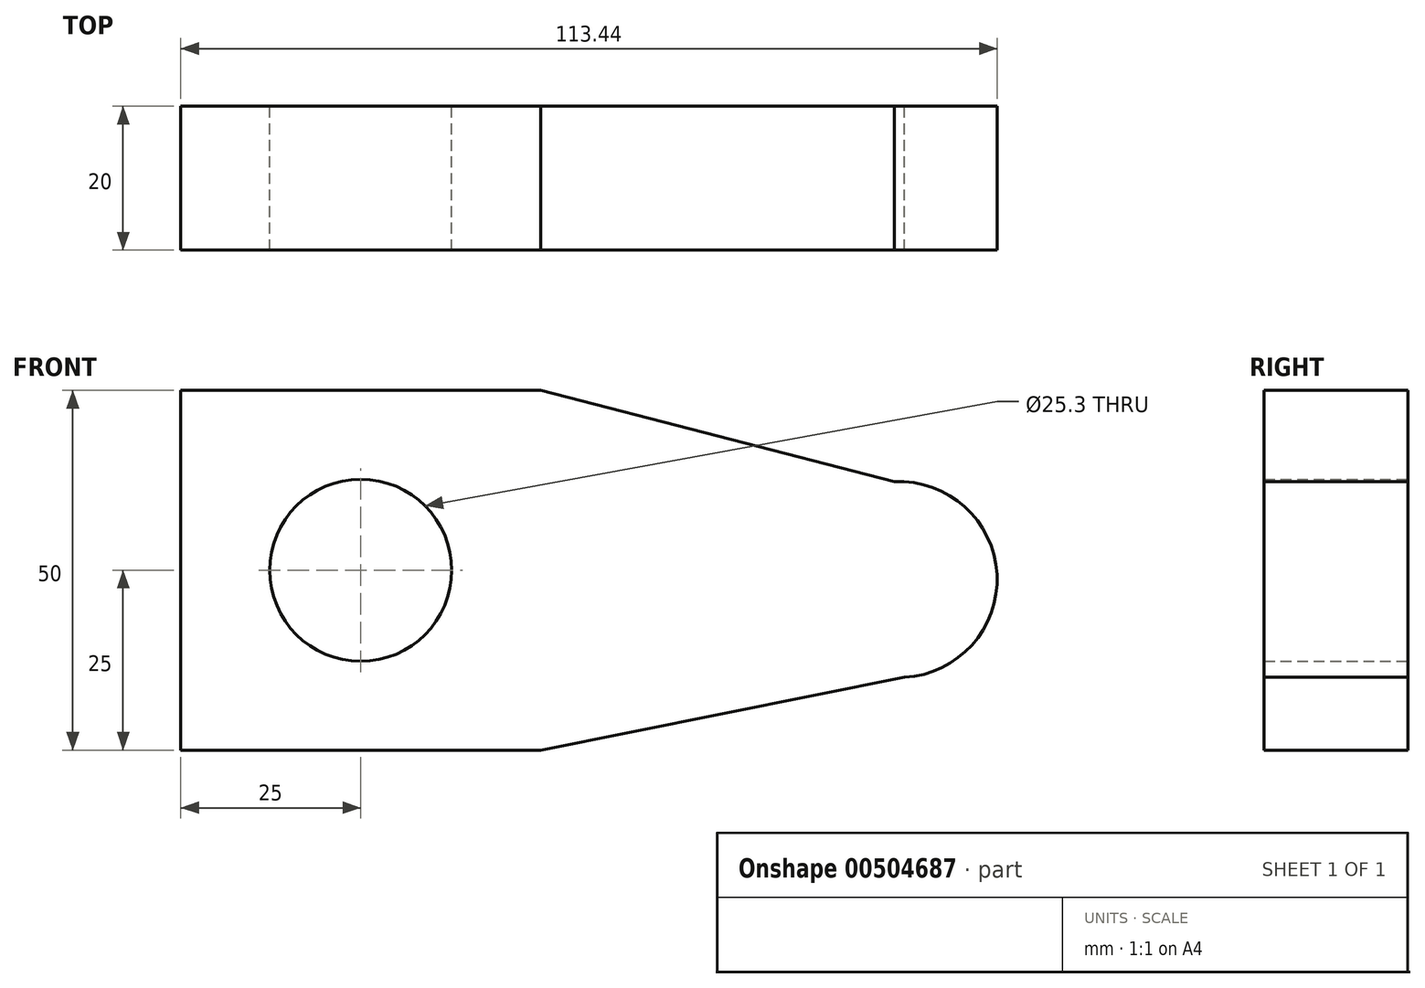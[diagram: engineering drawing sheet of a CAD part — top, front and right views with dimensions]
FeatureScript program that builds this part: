
annotation { "Feature Type Name" : "Feature", "Feature Type Description" : "" }
export const myFeature = defineFeature(function(context is Context, id is Id, definition is map)
    precondition{}
    {
        {
            var Q0;
            Q0=qCreatedBy(makeId("Front.planeOp"),FACE);
            var sketch = newSketch(context, id + "F0", { "sketchPlane" : qUnion([Q0])});
            skLineSegment(sketch, "E0.bottom", {"start": v(-25, 25) * mm, "end": v(25, 25) * mm});
            skLineSegment(sketch, "E0.top", {"start": v(-25, -25) * mm, "end": v(25, -25) * mm});
            skLineSegment(sketch, "E0.left", {"start": v(-25, 25) * mm, "end": v(-25, -25) * mm});
            skLineSegment(sketch, "E0.right", {"start": v(25, 25) * mm, "end": v(25, -25) * mm});
            skPoint(sketch, "E0.middle", {"position": v(0, 0) * mm});
            skCircle(sketch, "E1", {"center": v(0, 0) * mm, "radius": 12.65 * mm});
            skLineSegment(sketch, "E2.bottom", {"start": v(-25, 25) * mm, "end": v(-9, 25) * mm});
            skLineSegment(sketch, "E2.top", {"start": v(-25, 20) * mm, "end": v(-9, 20) * mm});
            skLineSegment(sketch, "E2.left", {"start": v(-25, 25) * mm, "end": v(-25, 20) * mm});
            skLineSegment(sketch, "E2.right", {"start": v(-9, 25) * mm, "end": v(-9, 20) * mm});
            skLineSegment(sketch, "E3.bottom", {"start": v(-25, -25) * mm, "end": v(-9, -25) * mm});
            skLineSegment(sketch, "E3.top", {"start": v(-25, -20) * mm, "end": v(-9, -20) * mm});
            skLineSegment(sketch, "E3.left", {"start": v(-25, -25) * mm, "end": v(-25, -20) * mm});
            skLineSegment(sketch, "E3.right", {"start": v(-9, -25) * mm, "end": v(-9, -20) * mm});
            skCircle(sketch, "E4", {"center": v(74.83, -1.3) * mm, "radius": 13.6 * mm});
            skLineSegment(sketch, "E5", {"start": v(25, 25) * mm, "end": v(74.13, 12.3) * mm});
            skLineSegment(sketch, "E6", {"start": v(25, -25) * mm, "end": v(75.54, -14.88) * mm});
            skSolve(sketch);
        }
        {
            var Q0;
            Q0 = qSketchRegion(id + "F0", true);
            extrude(context, id + "F1", {"entities" : qUnion([Q0]), "depth" : 20 * mm});
        }
    });
